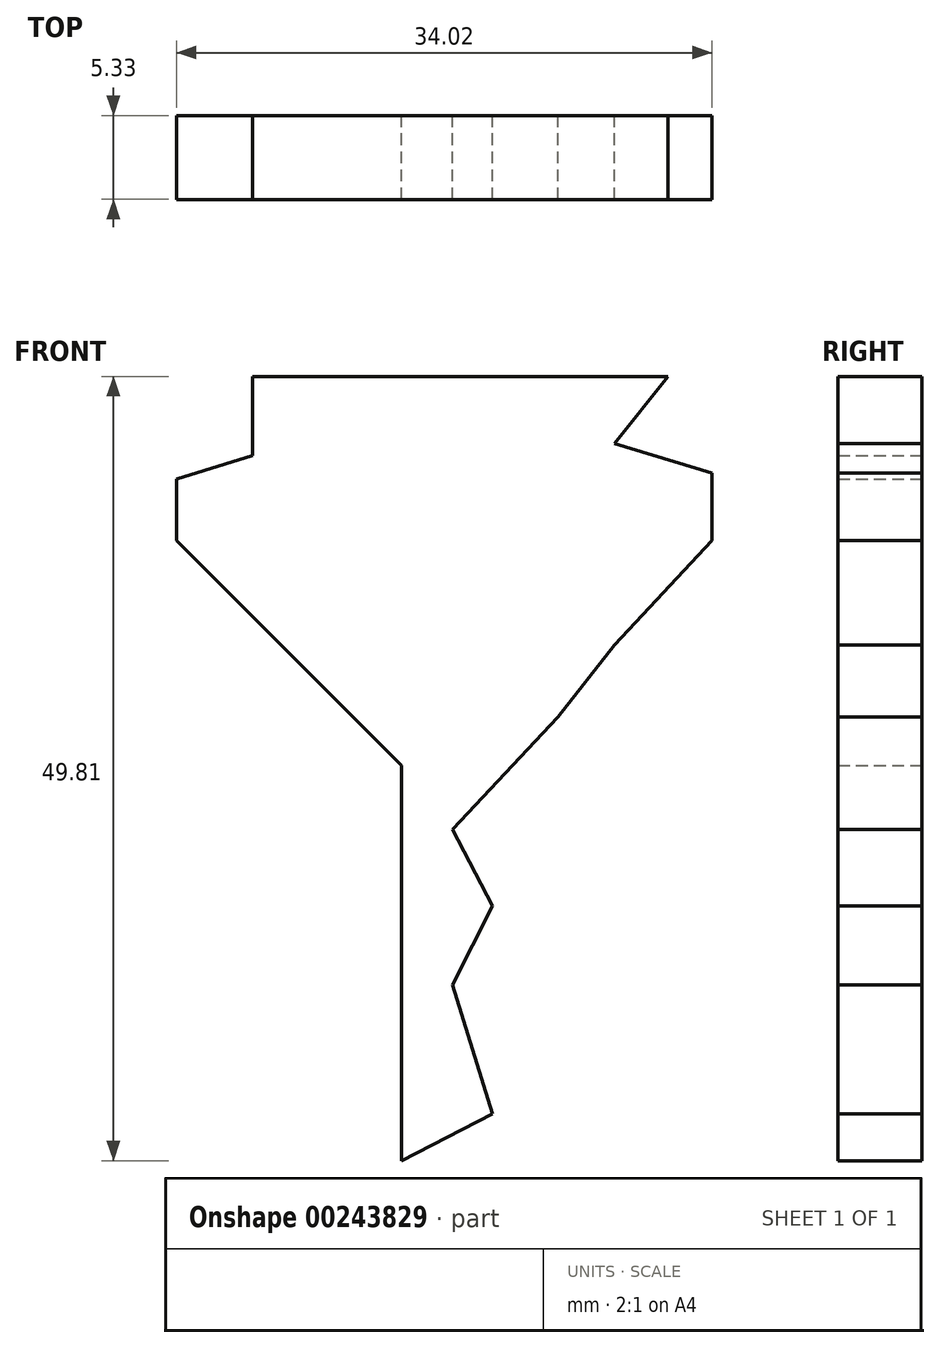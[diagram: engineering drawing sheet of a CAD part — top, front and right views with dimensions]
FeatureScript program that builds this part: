
annotation { "Feature Type Name" : "Feature", "Feature Type Description" : "" }
export const myFeature = defineFeature(function(context is Context, id is Id, definition is map)
    precondition{}
    {
        {
            var Q0;
            Q0=qCreatedBy(makeId("Front.planeOp"),FACE);
            var sketch = newSketch(context, id + "F0", { "sketchPlane" : qUnion([Q0])});
            skLineSegment(sketch, "E0", {"start": v(-8, 36.9) * mm, "end": v(-34.38, 36.9) * mm});
            skLineSegment(sketch, "E1", {"start": v(-34.38, 36.9) * mm, "end": v(-34.38, 31.87) * mm});
            skLineSegment(sketch, "E2", {"start": v(-34.38, 31.87) * mm, "end": v(-39.22, 30.39) * mm});
            skLineSegment(sketch, "E3", {"start": v(-39.22, 30.39) * mm, "end": v(-39.22, 26.48) * mm});
            skLineSegment(sketch, "E4", {"start": v(-39.22, 26.48) * mm, "end": v(-24.9, 12.17) * mm});
            skLineSegment(sketch, "E5", {"start": v(-24.9, 12.17) * mm, "end": v(-24.9, -12.92) * mm});
            skLineSegment(sketch, "E6", {"start": v(-24.9, -12.92) * mm, "end": v(-19.14, -9.94) * mm});
            skLineSegment(sketch, "E7", {"start": v(-19.14, -9.94) * mm, "end": v(-21.68, -1.75) * mm});
            skLineSegment(sketch, "E8", {"start": v(-21.68, -1.75) * mm, "end": v(-19.14, 3.25) * mm});
            skLineSegment(sketch, "E9", {"start": v(-19.14, 3.25) * mm, "end": v(-21.68, 8.1) * mm});
            skLineSegment(sketch, "E10", {"start": v(-21.68, 8.1) * mm, "end": v(-14.98, 15.25) * mm});
            skLineSegment(sketch, "E11", {"start": v(-14.98, 15.25) * mm, "end": v(-11.38, 19.84) * mm});
            skLineSegment(sketch, "E12", {"start": v(-11.38, 19.84) * mm, "end": v(-5.2, 26.48) * mm});
            skLineSegment(sketch, "E13", {"start": v(-5.2, 26.48) * mm, "end": v(-5.2, 30.76) * mm});
            skLineSegment(sketch, "E14", {"start": v(-5.2, 30.76) * mm, "end": v(-11.38, 32.62) * mm});
            skLineSegment(sketch, "E15", {"start": v(-11.38, 32.62) * mm, "end": v(-8, 36.9) * mm});
            skSolve(sketch);
        }
        {
            var Q0;
            Q0=makeQuery(id+"F0.imprint","IMPRINT",FACE,{"disambiguationData":[TD([[makeQuery(id+"F0.imprint","IMPRINT",EDGE,{"derivedFrom":sQuery(id+"F0.wireOp",EDGE,"E0")}),1.0]])]});
            extrude(context, id + "F1", {"entities" : qUnion([Q0]), "depth" : 5.33 * mm});
        }
    });
